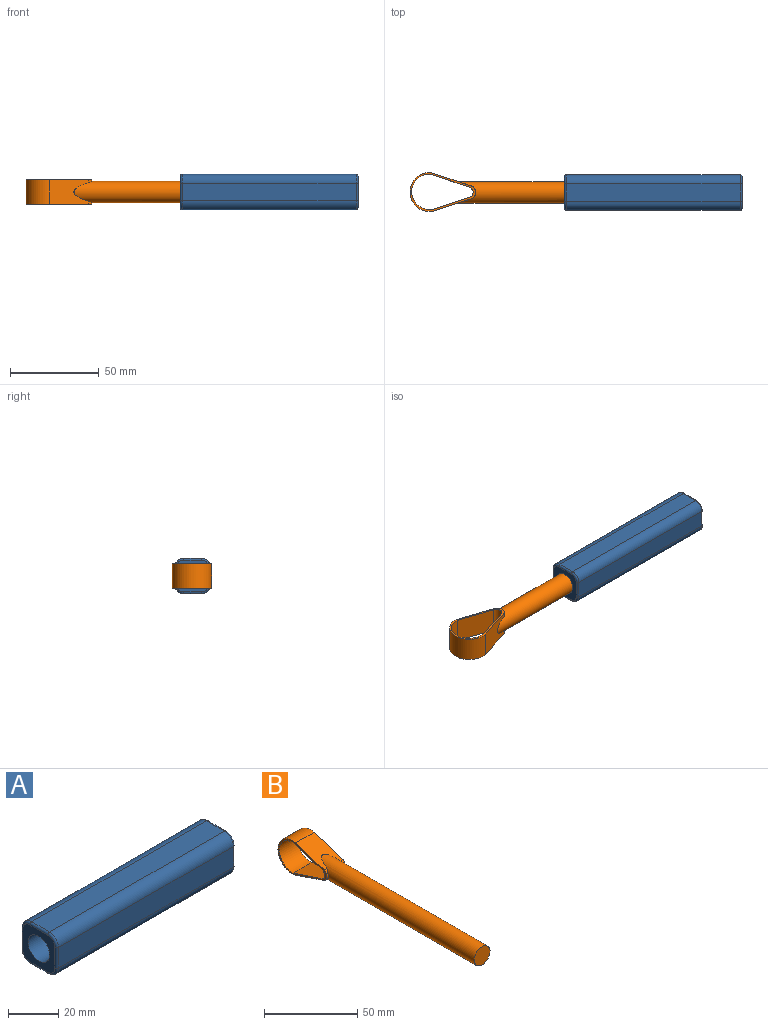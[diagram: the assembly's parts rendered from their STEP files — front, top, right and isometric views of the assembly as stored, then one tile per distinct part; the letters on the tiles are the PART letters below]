
ASSEMBLY  parts=2 mates=1
PART A: 27 faces, bbox 100x20.8x20.8 mm
  f0: plane 18x18mm, normal (-1,0,0), area 197.2mm2, adj f10,f11,f12,f13,f14,f15,f16,f17
  f1: plane 98x10mm, normal (0,0,-1), area 980mm2, adj f6,f8,f16,f23
  f2: plane 18x18mm, normal (1,0,0), area 197.2mm2, adj f18,f19,f20,f21,f22,f23,f24,f25
  f3: plane 98x10mm, normal (0,0,1), area 980mm2, adj f7,f9,f11,f20
  f4: plane 98x10mm, normal (0,-1,0), area 980mm2, adj f8,f9,f12,f19
  f5: plane 98x10mm, normal (0,1,0), area 980mm2, adj f6,f7,f15,f24
  f6: cylinder r=5mm len=98mm, axis (1,0,0), area 769.7mm2, adj f1,f5,f17,f25
  f7: cylinder r=5mm len=98mm, axis (-1,0,0), area 769.7mm2, adj f3,f5,f13,f22
  f8: cylinder r=5mm len=98mm, axis (-1,0,0), area 769.7mm2, adj f1,f4,f14,f21
  f9: cylinder r=5mm len=98mm, axis (1,0,0), area 769.7mm2, adj f3,f4,f10,f18
  f10: torus R=4mm, axis (-1,0,0), area 11.4mm2, adj f0,f9,f11,f12
  f11: cylinder r=1mm len=10mm, axis (0,1,0), area 15.7mm2, adj f0,f3,f10,f13
  f12: cylinder r=1mm len=10mm, axis (0,0,1), area 15.7mm2, adj f0,f4,f10,f14
  f13: torus R=4mm, axis (-1,0,0), area 11.4mm2, adj f0,f7,f11,f15
  f14: torus R=4mm, axis (-1,0,0), area 11.4mm2, adj f0,f8,f12,f16
  f15: cylinder r=1mm len=10mm, axis (0,0,-1), area 15.7mm2, adj f0,f5,f13,f17
  f16: cylinder r=1mm len=10mm, axis (0,-1,0), area 15.7mm2, adj f0,f1,f14,f17
  f17: torus R=4mm, axis (-1,0,0), area 11.4mm2, adj f0,f6,f15,f16
  f18: torus R=4mm, axis (-1,0,0), area 11.4mm2, adj f2,f9,f19,f20
  f19: cylinder r=1mm len=10mm, axis (0,0,-1), area 15.7mm2, adj f2,f4,f18,f21
  f20: cylinder r=1mm len=10mm, axis (0,-1,0), area 15.7mm2, adj f2,f3,f18,f22
  f21: torus R=4mm, axis (-1,0,0), area 11.4mm2, adj f2,f8,f19,f23
  f22: torus R=4mm, axis (-1,0,0), area 11.4mm2, adj f2,f7,f20,f24
  f23: cylinder r=1mm len=10mm, axis (0,1,0), area 15.7mm2, adj f1,f2,f21,f25
  f24: cylinder r=1mm len=10mm, axis (0,0,1), area 15.7mm2, adj f2,f5,f22,f25
  f25: torus R=4mm, axis (-1,0,0), area 11.4mm2, adj f2,f6,f23,f24
  f26: cylinder r=6mm len=100mm, axis (-1,0,0), area 3769.9mm2, adj f0,f2
PART B: 13 faces, bbox 14x147.7x22 mm
  f0: plane 37x22mm, normal (-1,0,0), area 92.8mm2, adj f3,f4,f5,f6,f9,f10,f11,f12
  f1: plane 37x22mm, normal (1,0,0), area 92.8mm2, adj f2,f4,f5,f6,f9,f10,f11,f12
  f2: cylinder r=4mm len=7.48mm, axis (1,0,0), area 15.9mm2, adj f1,f4,f5,f7
  f3: cylinder r=4mm len=7.48mm, axis (1,0,0), area 15.9mm2, adj f0,f4,f5,f7
  f4: plane 21.51x14mm, normal (0,-0.31,0.95), area 259.3mm2, adj f0,f1,f2,f3,f6,f7
  f5: plane 21.86x14mm, normal (0,-0.32,-0.95), area 284.2mm2, adj f0,f1,f2,f3,f6,f7
  f6: cylinder r=11mm len=22mm, axis (1,0,0), area 526.4mm2, adj f0,f1,f4,f5
  f7: cylinder r=6mm len=120.69mm, axis (0,1,0), area 4343.7mm2, adj f2,f3,f4,f5,f8
  f8: plane 12x12mm, normal (0,-1,0), area 113.1mm2, adj f7
  f9: plane 21.58x14mm, normal (0,0.31,-0.95), area 317.4mm2, adj f0,f1,f10,f12
  f10: cylinder r=3.16mm len=14mm, axis (-1,0,0), area 97.4mm2, adj f0,f1,f9,f11
  f11: plane 21.78x14mm, normal (0,0.32,0.95), area 321.5mm2, adj f0,f1,f10,f12
  f12: cylinder r=9.99mm len=19.98mm, axis (-1,0,0), area 472.4mm2, adj f0,f1,f9,f11
PLACE A t=(-30.72,17.55,-15.37)mm
PLACE B rot(axis=(0.58,-0.58,0.58),120deg) t=(-92.02,7.55,-5.37)mm
MATE parallel B.f7 <-> A.f26  axis (-1,0,0) through (-30.72,7.55,-5.37)mm
